# Revit family: Sanitary_Taps-Mixers_hansgrohe_72213XXX-Rebris-E-Single-lever-bidet-mix_YYYY
name_source: partatom
category: Plumbing Fixtures
revit_build: Autodesk Revit 2018 (Build: 20170223_1515(x64)
units: mm (PartAtom-declared; Revit-internal decimal feet)

## family parameters
Always vertical = No
Cut with Voids When Loaded = No
OmniClass Number = 23.45.55.17
OmniClass Title = Mixing Faucets
Part Type = Normal
Room Calculation Point = No
Round Connector Dimension = Use Diameter
Shared = No
Work Plane-Based = Yes

## types (2) — shared parameters
BIMobject category = Taps & Mixers
Cold Water  Inlet = 10 mm
Cold Water Inlet Description = Cold Water  Inlet 9.5 mm
Default Elevation = 1219.2 mm  [stored 4 ft]
Description = Rebris E Single lever bidet mixer with metal pop-up waste set
Design country = Germany
EAN code = 4059625413050
Edition number = 1
GTIN code = https://4059625402146
Hot Water Inlet = 10 mm
Hot Water Inlet Description = Hot Water  Inlet 9.5 mm
IFC Classification = Valve
Manufacturer = Hansgrohe
Manufacturer country = Germany
Manufacturer name = hansgrohe
Model = 72213XXX
OmniClass Code = 23-31 11 00
OmniClass Description = Faucets
Product Guid = 2ec8763f-e5a1-44b0-ac8a-525ac042dad2
Product SKU = 72213XXX
Product data url = https://bimobject.com
Product family = Rebris E
Product group = Bidet mixers
Product name = 72213XXX Rebris E Single lever bidet mixer with metal pop-up waste set
QR code = https://bimobject.com
UNSPSC Code = 301815
URL = https://www.hansgrohe.com
Weight Net (Kg) = 1.9

## per-type parameters (varying)
| type | Material 1 |
| 000 Chrome | Hansgrohe - Metal - 000 Chrome |
| 670 Matte Black | Hansgrohe - Metal - 670 Matte Black |

note: [stored X ft] marks values corroborated as IEEE doubles in the binary element streams (Revit-internal decimal feet)

## geometry (parser evidence)
native form markers: Sweep x3
no freeform markers — native parametric forms only
